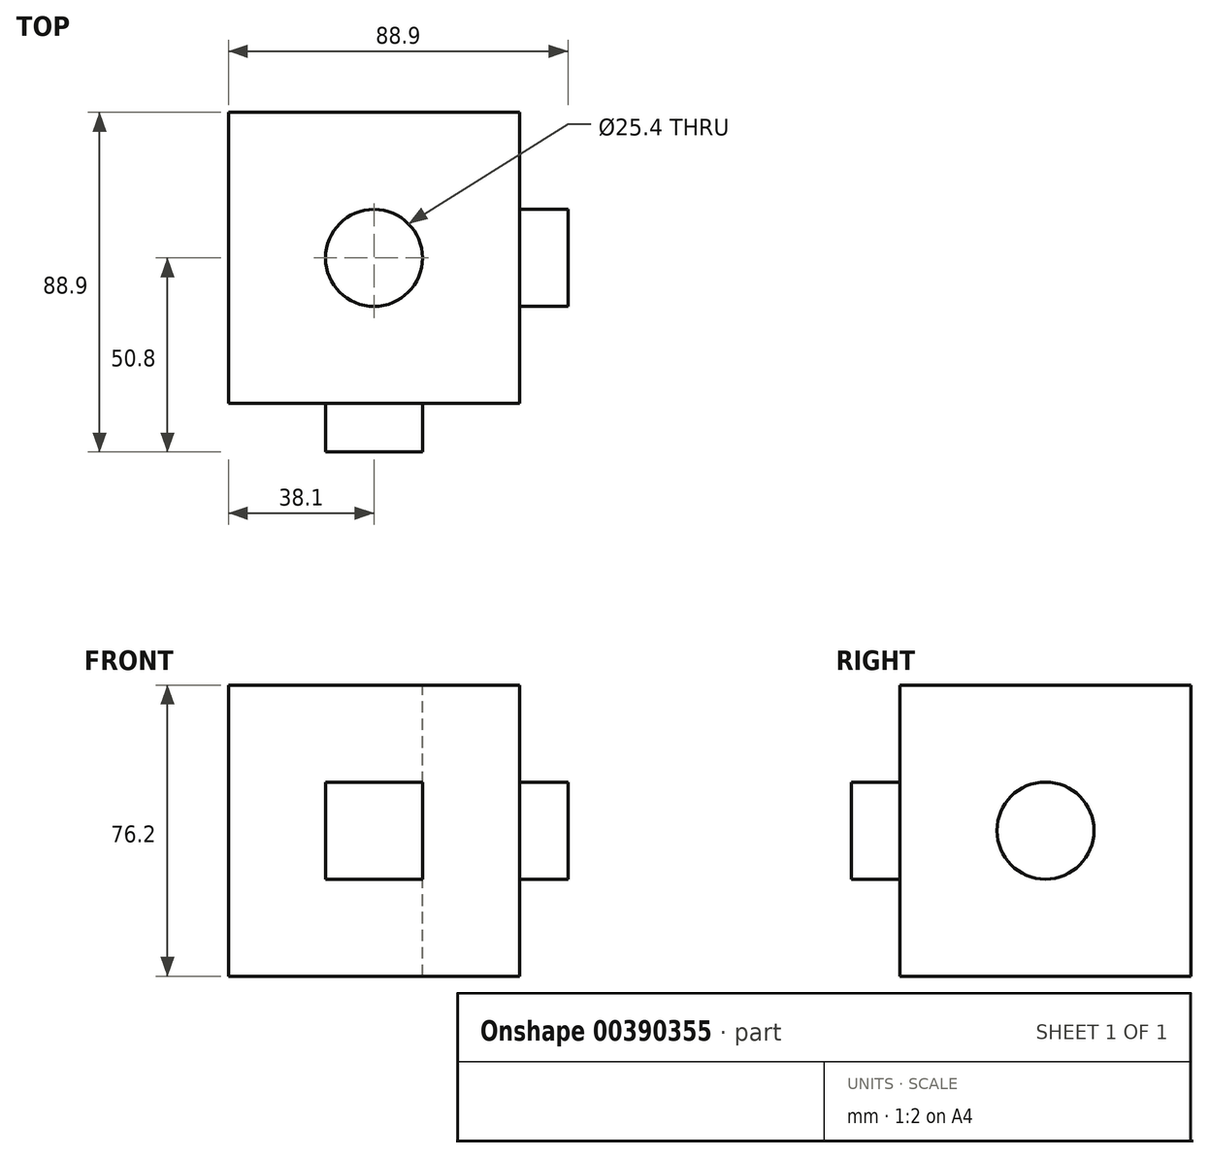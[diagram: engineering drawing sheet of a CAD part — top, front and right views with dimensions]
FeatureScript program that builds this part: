
annotation { "Feature Type Name" : "Feature", "Feature Type Description" : "" }
export const myFeature = defineFeature(function(context is Context, id is Id, definition is map)
    precondition{}
    {
        {
            var Q0;
            Q0=qCreatedBy(makeId("Front.planeOp"),FACE);
            var sketch = newSketch(context, id + "F0", { "sketchPlane" : qUnion([Q0])});
            skLineSegment(sketch, "E0.bottom", {"start": v(0.26, 4.63) * mm, "end": v(76.46, 4.63) * mm});
            skLineSegment(sketch, "E0.top", {"start": v(0.26, -71.57) * mm, "end": v(76.46, -71.57) * mm});
            skLineSegment(sketch, "E0.left", {"start": v(0.26, 4.63) * mm, "end": v(0.26, -71.57) * mm});
            skLineSegment(sketch, "E0.right", {"start": v(76.46, 4.63) * mm, "end": v(76.46, -71.57) * mm});
            skPoint(sketch, "E0.middle", {"position": v(38.36, -33.47) * mm});
            skSolve(sketch);
        }
        {
            var Q0;
            Q0=makeQuery(id+"F0.imprint","IMPRINT",FACE,{"disambiguationData":[TD([[makeQuery(id+"F0.imprint","IMPRINT",EDGE,{"derivedFrom":sQuery(id+"F0.wireOp",EDGE,"E0.bottom")}),-1.0]])]});
            extrude(context, id + "F1", {"entities" : qUnion([Q0]), "depth" : 76.2 * mm});
        }
        {
            var Q0;
            Q0=makeQuery(id+"F1.opExtrude","SWEPT_FACE",FACE,{"disambiguationData":[OSD([sQuery(id+"F0.wireOp",EDGE,"E0.bottom")])]});
            var sketch = newSketch(context, id + "F2", { "sketchPlane" : qUnion([Q0])});
            skPoint(sketch, "E1", {"position": v(38.36, -38.1) * mm});
            skSolve(sketch);
        }
        {
            var Q0;
            Q0=sQuery(id+"F2.wireOp",VERTEX,"E1");
            var Q1;
            Q1=makeQuery(id+"F1.opExtrude","SWEPT_BODY",BODY,{"disambiguationData":[OSD([sQuery(id+"F0.wireOp",EDGE,"E0.bottom"),sQuery(id+"F0.wireOp",EDGE,"E0.top"),sQuery(id+"F0.wireOp",EDGE,"E0.left"),sQuery(id+"F0.wireOp",EDGE,"E0.right")])]});
            hole(context, id + "F3", {"style" : HoleStyle.SIMPLE, "endStyle" : HoleEndStyle.THROUGH, "holeDiameter" : 25.4 * mm, "isTappedThrough" : true, "tappedDepth" : 12.7 * mm, "tapClearance" : 3, "locations" : qUnion([Q0]), "scope" : qUnion([Q1])});
        }
        {
            var Q0;
            Q0=makeQuery(id+"F1.opExtrude","CAP_FACE",FACE,{"disambiguationData":[OSD([sQuery(id+"F0.wireOp",EDGE,"E0.bottom"),sQuery(id+"F0.wireOp",EDGE,"E0.top"),sQuery(id+"F0.wireOp",EDGE,"E0.left"),sQuery(id+"F0.wireOp",EDGE,"E0.right")])],"isStart":false});
            var sketch = newSketch(context, id + "F4", { "sketchPlane" : qUnion([Q0])});
            skLineSegment(sketch, "E2.bottom", {"start": v(51.06, -46.17) * mm, "end": v(25.66, -46.17) * mm});
            skLineSegment(sketch, "E2.top", {"start": v(51.06, -20.77) * mm, "end": v(25.66, -20.77) * mm});
            skLineSegment(sketch, "E2.left", {"start": v(51.06, -46.17) * mm, "end": v(51.06, -20.77) * mm});
            skLineSegment(sketch, "E2.right", {"start": v(25.66, -46.17) * mm, "end": v(25.66, -20.77) * mm});
            skPoint(sketch, "E2.middle", {"position": v(38.36, -33.47) * mm});
            skSolve(sketch);
        }
        {
            var Q0;
            Q0=makeQuery(id+"F4.imprint","IMPRINT",FACE,{"disambiguationData":[TD([[makeQuery(id+"F4.imprint","IMPRINT",EDGE,{"derivedFrom":sQuery(id+"F4.wireOp",EDGE,"E2.bottom")}),-1.0]])]});
            extrude(context, id + "F5", {"entities" : qUnion([Q0]), "operationType" : NewBodyOperationType.ADD, "depth" : 12.7 * mm});
        }
        {
            var Q0;
            Q0=makeQuery(id+"F1.opExtrude","SWEPT_FACE",FACE,{"disambiguationData":[OSD([sQuery(id+"F0.wireOp",EDGE,"E0.right")])]});
            var sketch = newSketch(context, id + "F6", { "sketchPlane" : qUnion([Q0])});
            skCircle(sketch, "E3", {"center": v(-38.1, -33.47) * mm, "radius": 12.7 * mm});
            skSolve(sketch);
        }
        {
            var Q0;
            Q0 = qSketchRegion(id + "F6", true);
            extrude(context, id + "F7", {"entities" : qUnion([Q0]), "operationType" : NewBodyOperationType.ADD, "depth" : 12.7 * mm});
        }
    });
